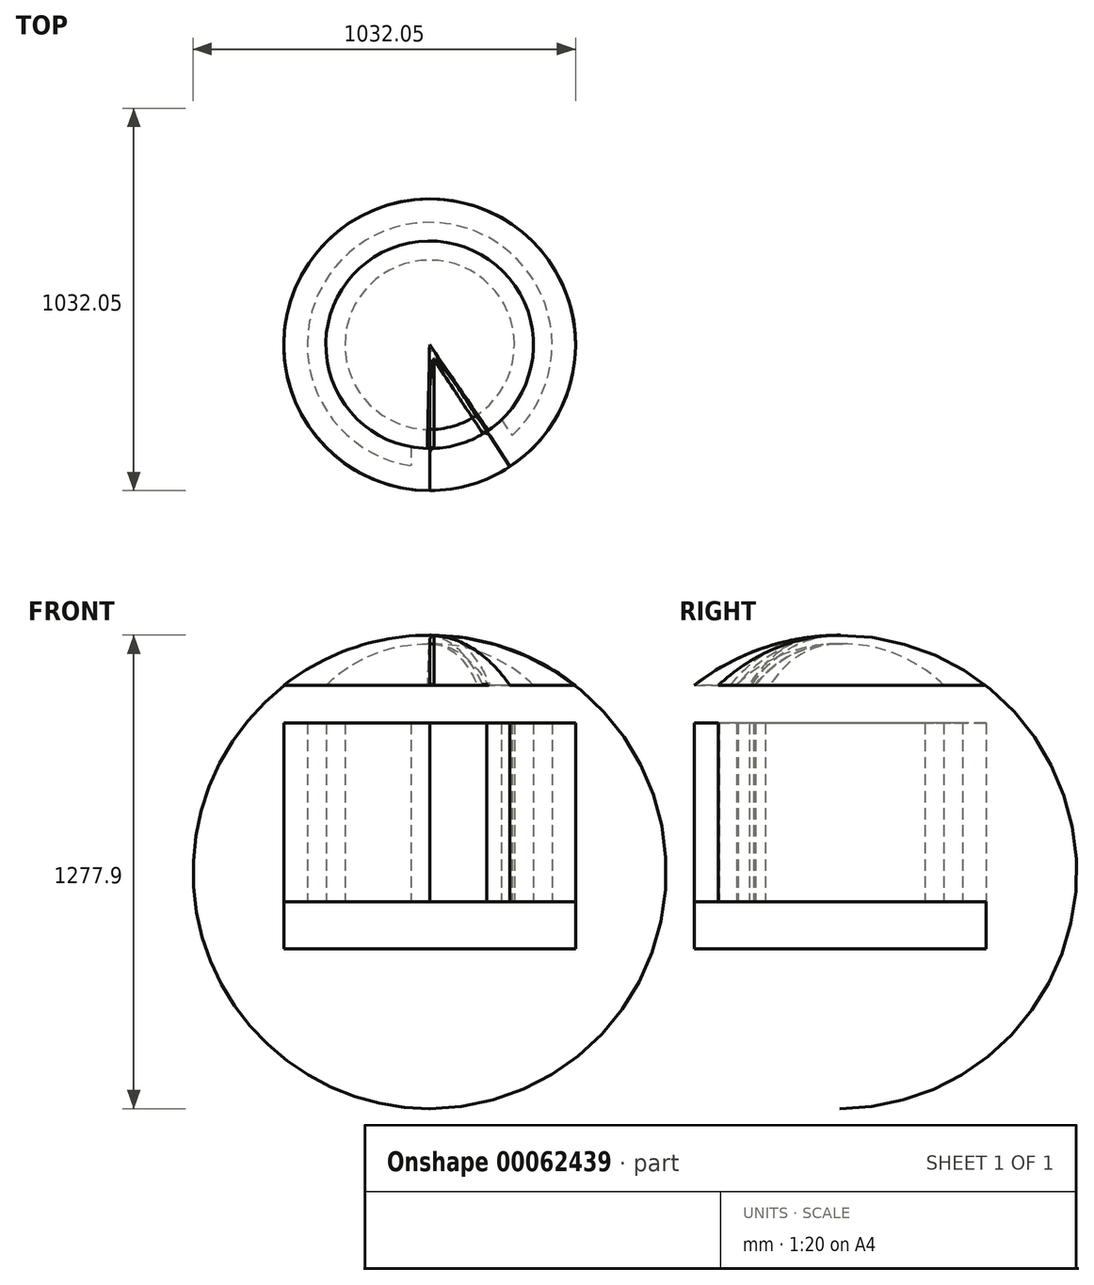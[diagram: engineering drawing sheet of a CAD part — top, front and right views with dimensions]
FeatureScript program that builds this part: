
annotation { "Feature Type Name" : "Feature", "Feature Type Description" : "" }
export const myFeature = defineFeature(function(context is Context, id is Id, definition is map)
    precondition{}
    {
        {
            var Q0;
            Q0=qCreatedBy(makeId("Top.planeOp"),FACE);
            var sketch = newSketch(context, id + "F0", { "sketchPlane" : qUnion([Q0])});
            skCircle(sketch, "E0", {"center": v(0, 0) * mm, "radius": 393.7 * mm});
            skSolve(sketch);
        }
        {
            var Q0;
            Q0=makeQuery(id+"F0.imprint","IMPRINT",FACE,{"disambiguationData":[TD([[makeQuery(id+"F0.imprint","IMPRINT",EDGE,{"derivedFrom":sQuery(id+"F0.wireOp",EDGE,"E0")}),1.0]])]});
            extrude(context, id + "F1", {"entities" : qUnion([Q0]), "depth" : 127 * mm});
        }
        {
            var Q0;
            Q0=makeQuery(id+"F1.opExtrude","CAP_FACE",FACE,{"disambiguationData":[OSD([sQuery(id+"F0.wireOp",EDGE,"E0")])],"isStart":false});
            var sketch = newSketch(context, id + "F2", { "sketchPlane" : qUnion([Q0])});
            skArc(sketch, "E1", {"start": v(222.07, -244.37) * mm, "mid": v(-94.93, 316.26) * mm, "end": v(-50.8, -326.27) * mm});
            skArc(sketch, "E2", {"start": v(216.8, -328.63) * mm, "mid": v(-113.18, 377.08) * mm, "end": v(0, -393.7) * mm});
            skCircle(sketch, "E3", {"center": v(0, 0) * mm, "radius": 228.6 * mm});
            skArc(sketch, "E4", {"start": v(193.7, -201.36) * mm, "mid": v(-80.32, 267.6) * mm, "end": v(-50.8, -274.74) * mm});
            skLineSegment(sketch, "E5", {"start": v(0, -279.55) * mm, "end": v(0, -393.7) * mm});
            skLineSegment(sketch, "E6", {"start": v(153.94, -233.34) * mm, "end": v(216.8, -328.63) * mm});
            skLineSegment(sketch, "E7", {"start": v(-50.8, -274.74) * mm, "end": v(-50.8, -326.27) * mm});
            skLineSegment(sketch, "E8", {"start": v(193.7, -201.36) * mm, "end": v(222.07, -244.37) * mm});
            skArc(sketch, "E9", {"start": v(0, -279.55) * mm, "mid": v(80.4, -267.84) * mm, "end": v(153.94, -233.34) * mm});
            skSolve(sketch);
        }
        {
            var Q0;
            Q0=makeQuery(id+"F2.imprint","IMPRINT",FACE,{"disambiguationData":[TD([[makeQuery(id+"F2.imprint","IMPRINT",EDGE,{"derivedFrom":sQuery(id+"F2.wireOp",EDGE,"E1")}),-1.0]])]});
            extrude(context, id + "F3", {"entities" : qUnion([Q0]), "depth" : 482.6 * mm});
        }
        {
            var Q0;
            Q0=qCreatedBy(makeId("Right.planeOp"),FACE);
            var sketch = newSketch(context, id + "F4", { "sketchPlane" : qUnion([Q0])});
            skLineSegment(sketch, "E10", {"start": v(0, 823.11) * mm, "end": v(0, 846.49) * mm});
            skLineSegment(sketch, "E11", {"start": v(-393.59, 711.2) * mm, "end": v(-280.14, 711.2) * mm});
            skArc(sketch, "E12", {"start": v(0, 846.49) * mm, "mid": v(-208.12, 811.8) * mm, "end": v(-393.59, 711.2) * mm});
            skArc(sketch, "E13", {"start": v(0, 823.11) * mm, "mid": v(-151.4, 795.5) * mm, "end": v(-280.14, 711.2) * mm});
            skPoint(sketch, "E14.orphan", {"position": v(0, 0) * mm});
            skSolve(sketch);
        }
        {
            var Q0;
            Q0=makeQuery(id+"F4.imprint","IMPRINT",FACE,{"disambiguationData":[TD([[makeQuery(id+"F4.imprint","IMPRINT",EDGE,{"derivedFrom":sQuery(id+"F4.wireOp",EDGE,"E10")}),1.0]])]});
            var Q1;
            Q1=sQuery(id+"F4.wireOp",EDGE,"E10");
            revolve(context, id + "F5", {"entities" : qUnion([Q0]), "axis" : qUnion([Q1]), "revolveType" : RevolveType.ONE_DIRECTION, "oppositeDirection" : true, "angle" : 5.7 * radian});
        }
        {
            var Q0;
            Q0=qCreatedBy(makeId("Right.planeOp"),FACE);
            var sketch = newSketch(context, id + "F6", { "sketchPlane" : qUnion([Q0])});
            skLineSegment(sketch, "E15", {"start": v(-279.95, 710.8) * mm, "end": v(-228.67, 710.8) * mm});
            skLineSegment(sketch, "E16", {"start": v(0, 822.78) * mm, "end": v(0, 846.75) * mm});
            skArc(sketch, "E17", {"start": v(0, 846.75) * mm, "mid": v(-155.46, 810.67) * mm, "end": v(-279.95, 710.8) * mm});
            skArc(sketch, "E18", {"start": v(0, 822.78) * mm, "mid": v(-128.21, 795.14) * mm, "end": v(-228.67, 710.8) * mm});
            skPoint(sketch, "E19.start.orphan", {"position": v(0, 792.12) * mm});
            skPoint(sketch, "E20", {"position": v(0, 846.75) * mm});
            skSolve(sketch);
        }
        {
            var Q0;
            Q0=makeQuery(id+"F6.imprint","IMPRINT",FACE,{"disambiguationData":[TD([[makeQuery(id+"F6.imprint","IMPRINT",EDGE,{"derivedFrom":sQuery(id+"F6.wireOp",EDGE,"E15")}),1.0]])]});
            var Q1;
            Q1=sQuery(id+"F6.wireOp",EDGE,"E16");
            revolve(context, id + "F7", {"entities" : qUnion([Q0]), "axis" : qUnion([Q1]), "revolveType" : RevolveType.TWO_DIRECTIONS, "angle" : .6 * radian, "angleBack" : 6.26 * radian});
        }
        {
            var Q0;
            Q0=makeQuery(id+"F5.opRevolve","SWEPT_BODY",BODY,{"disambiguationData":[OSD([sQuery(id+"F4.wireOp",EDGE,"E10"),sQuery(id+"F4.wireOp",EDGE,"E11"),sQuery(id+"F4.wireOp",EDGE,"E12"),sQuery(id+"F4.wireOp",EDGE,"E13")])]});
            var Q1;
            Q1=makeQuery(id+"F7.opRevolve","SWEPT_BODY",BODY,{"disambiguationData":[OSD([sQuery(id+"F6.wireOp",EDGE,"E15"),sQuery(id+"F6.wireOp",EDGE,"E16"),sQuery(id+"F6.wireOp",EDGE,"E17"),sQuery(id+"F6.wireOp",EDGE,"E18")])]});
            booleanBodies(context, id + "F8", {"operationType" : BooleanOperationType.UNION, "tools" : qUnion([Q0, Q1])});
        }
        {
            var Q0;
            Q0=makeQuery(id+"F8.opBoolean","INTERSECT",EDGE,{"derivedFrom":[makeQuery(id+"F5.opRevolve","CAP_FACE",FACE,{"disambiguationData":[OSD([sQuery(id+"F4.wireOp",EDGE,"E10"),sQuery(id+"F4.wireOp",EDGE,"E11"),sQuery(id+"F4.wireOp",EDGE,"E12"),sQuery(id+"F4.wireOp",EDGE,"E13")])],"isStart":true}),makeQuery(id+"F7.opRevolve","SWEPT_FACE",FACE,{"disambiguationData":[OSD([sQuery(id+"F6.wireOp",EDGE,"E17")])]})]});
            fillet(context, id + "F9", {"entities" : qUnion([Q0]), "radius" : 12.7 * mm, "tangentPropagation" : true, "allowEdgeOverflow" : false});
        }
        {
            var Q0;
            Q0=makeQuery(id+"F8.opBoolean","INTERSECT",EDGE,{"derivedFrom":[makeQuery(id+"F5.opRevolve","CAP_FACE",FACE,{"disambiguationData":[OSD([sQuery(id+"F4.wireOp",EDGE,"E10"),sQuery(id+"F4.wireOp",EDGE,"E11"),sQuery(id+"F4.wireOp",EDGE,"E12"),sQuery(id+"F4.wireOp",EDGE,"E13")])],"isStart":false}),makeQuery(id+"F7.opRevolve","SWEPT_FACE",FACE,{"disambiguationData":[OSD([sQuery(id+"F6.wireOp",EDGE,"E17")])]})]});
            fillet(context, id + "F10", {"entities" : qUnion([Q0]), "radius" : 12.7 * mm, "tangentPropagation" : true, "allowEdgeOverflow" : false});
        }
    });
